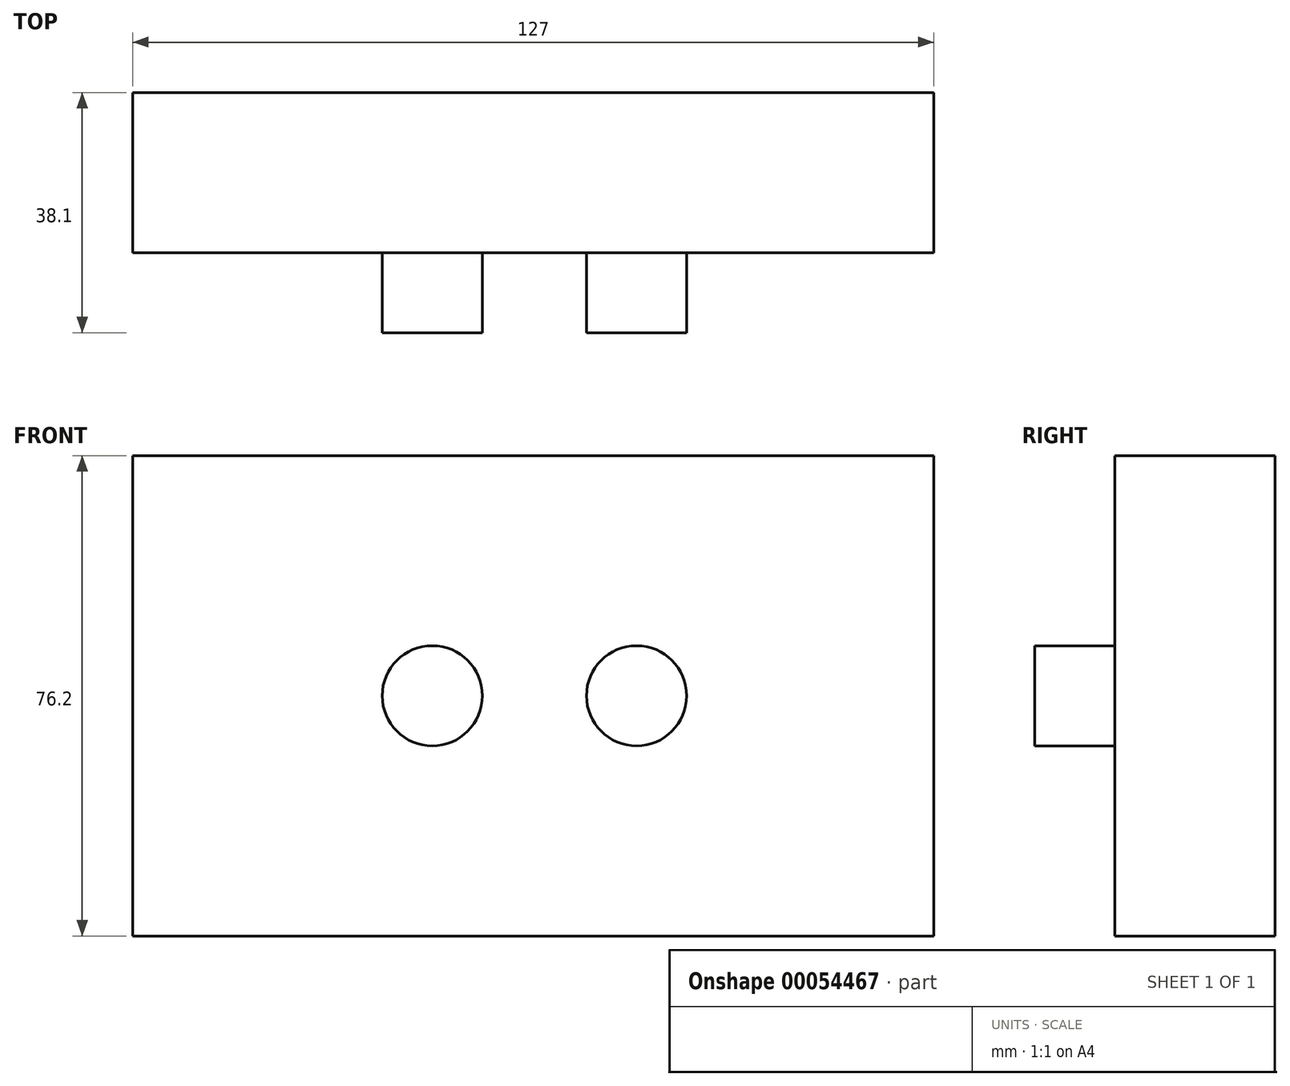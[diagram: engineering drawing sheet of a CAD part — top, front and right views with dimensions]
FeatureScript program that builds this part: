
annotation { "Feature Type Name" : "Feature", "Feature Type Description" : "" }
export const myFeature = defineFeature(function(context is Context, id is Id, definition is map)
    precondition{}
    {
        {
            var Q0;
            Q0=qCreatedBy(makeId("Front.planeOp"),FACE);
            var sketch = newSketch(context, id + "F0", { "sketchPlane" : qUnion([Q0])});
            skLineSegment(sketch, "E0.rect.bottom", {"start": v(63.5, 38.1) * mm, "end": v(-63.5, 38.1) * mm});
            skLineSegment(sketch, "E0.rect.top", {"start": v(63.5, -38.1) * mm, "end": v(-63.5, -38.1) * mm});
            skLineSegment(sketch, "E0.rect.left", {"start": v(63.5, 38.1) * mm, "end": v(63.5, -38.1) * mm});
            skLineSegment(sketch, "E0.rect.right", {"start": v(-63.5, 38.1) * mm, "end": v(-63.5, -38.1) * mm});
            skPoint(sketch, "E0.rect.middle", {"position": v(0, 0) * mm});
            skSolve(sketch);
        }
        {
            var Q0;
            Q0 = qSketchRegion(id + "F0", true);
            extrude(context, id + "F1", {"entities" : qUnion([Q0]), "oppositeDirection" : true, "depth" : 25.4 * mm});
        }
        {
            var Q0;
            Q0=qCreatedBy(makeId("Front.planeOp"),FACE);
            var sketch = newSketch(context, id + "F2", { "sketchPlane" : qUnion([Q0])});
            skLineSegment(sketch, "E1", {"start": v(-16, 19.18) * mm, "end": v(-16, -19.18) * mm, "construction": true});
            skLineSegment(sketch, "E2", {"start": v(16.38, 19.65) * mm, "end": v(16.38, -19.86) * mm, "construction": true});
            skLineSegment(sketch, "E3", {"start": v(0, 0) * mm, "end": v(-22.04, 0) * mm, "construction": true});
            skPoint(sketch, "E3.endSnap0", {"position": v(-16, 0) * mm});
            skLineSegment(sketch, "E4", {"start": v(-22.04, 0) * mm, "end": v(0, 0) * mm, "construction": true});
            skLineSegment(sketch, "E5", {"start": v(0, 0) * mm, "end": v(20.52, 0) * mm, "construction": true});
            skCircle(sketch, "E6", {"center": v(-16, 0) * mm, "radius": 7.94 * mm});
            skCircle(sketch, "E7", {"center": v(16.38, 0) * mm, "radius": 7.94 * mm});
            skSolve(sketch);
        }
        {
            var Q0;
            Q0=makeQuery(id+"F2.imprint","IMPRINT",FACE,{"disambiguationData":[TD([[makeQuery(id+"F2.imprint","IMPRINT",EDGE,{"derivedFrom":sQuery(id+"F2.wireOp",EDGE,"E6")}),1.0]])]});
            var Q1;
            Q1=makeQuery(id+"F2.imprint","IMPRINT",FACE,{"disambiguationData":[TD([[makeQuery(id+"F2.imprint","IMPRINT",EDGE,{"derivedFrom":sQuery(id+"F2.wireOp",EDGE,"E7")}),1.0]])]});
            extrude(context, id + "F3", {"entities" : qUnion([Q0, Q1]), "operationType" : NewBodyOperationType.ADD, "depth" : 12.7 * mm});
        }
    });
